# Revit family: IS_Softmood_T5192_BIM_GB
name_source: partatom
category: Plumbing Fixtures
revit_build: Autodesk Revit MEP 2014 (Build: 20130308_1515(x64)
units: mm (PartAtom-declared; Revit-internal decimal feet)

## types (1)
- T519201 - Softmood Bidet - Floor Standing
    Accessories = www.idealspec.co.uk
    AreaUnits = millimeters
    Assembly Code = C1030200
    AssetType = Fixed
    BIMObjectName = ISI_IdealStandard_Bidets_SoftMood_T5192
    BarCode = 8014140386223
    Brand = Ideal Standard
    CWFU = 0
    CodePerformance = Vitreous china to BS 3402
    Color = White
    ConnectionType = Plumbing
    Cost = 0 $
    Default Elevation = 0 mm  [stored 0 ft]
    Description = Softmood floor standing bidet.
    DrainSize = 0 mm  [stored 0 ft]
    DurationUnit = year
    ECA = No
    ExpectedLife = 30
    Features = Floor standing bidet.
    Finish = White
    HWFU = 0
    Help = www.idealspec.co.uk/contact-us.html
    IfcExportAs = IfcSanitaryTerminalType
    IfcExportType = WASHHANDBASIN
    InstallationInstructions = www.idealspec.co.uk/resources.html
    LinearUnits = millimeters
    ManufacturerURL = www.idealspec.co.uk
    Material = Vitreous China
    Model = T519201
    ModelNumber = T519201
    ModelReference = Softmood floor standing bidet.
    NBSDescription = Bidets
    NBSReference = 45-35-70/320
    Name = Bidets_SoftMood_T5192_IdealStandard
    NettWeight = 24.2 Kg
    NominalDepth = 560 mm
    NominalHeight = 420 mm  [stored 1.37795 ft]
    NominalLength = 0 mm  [stored 0 ft]
    NominalWidth = 361 mm
    ProductInformation = www.idealspec.co.uk/assets/datasheet/T519201
    Shape = Sculptured
    Size = 561 x 420 x 361 mm
    Space = Internal
    URL = www.idealspec.co.uk
    Uniclass2015Code = Pr_40_20_06_11
    Uniclass2015Title = Bidets
    Uniclass2015Version = Products v1.1
    Version = 1
    VolumeUnits = Litres
    WFU = 0
    WarrantyDescription = Manufacturers Warranty
    WarrantyDurationParts = 99
    WarrantyDurationUnit = year

note: [stored X ft] marks values corroborated as IEEE doubles in the binary element streams (Revit-internal decimal feet)

## geometry (parser evidence)
native form markers: Sweep x6
no freeform markers — native parametric forms only
